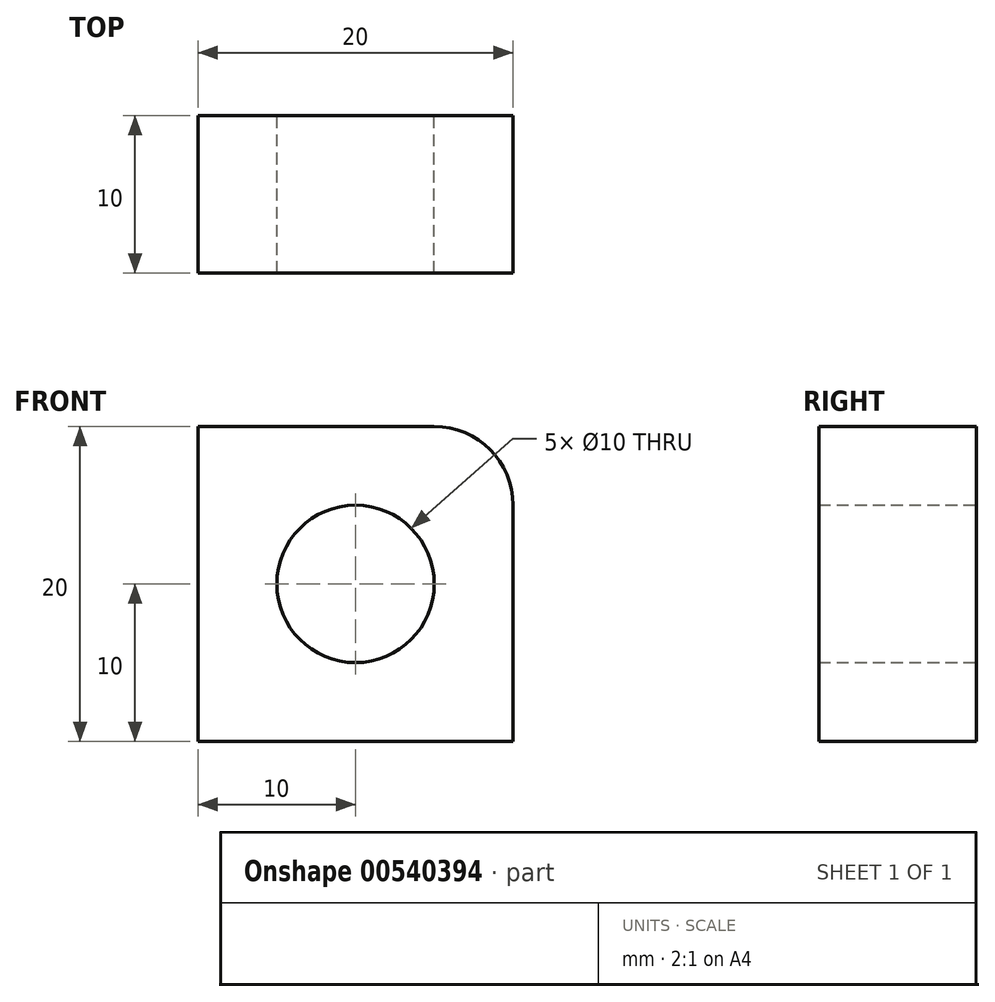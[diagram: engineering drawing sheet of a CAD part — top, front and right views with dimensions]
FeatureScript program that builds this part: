
annotation { "Feature Type Name" : "Feature", "Feature Type Description" : "" }
export const myFeature = defineFeature(function(context is Context, id is Id, definition is map)
    precondition{}
    {
        {
            var Q0;
            Q0=qCreatedBy(makeId("Front.planeOp"),FACE);
            var sketch = newSketch(context, id + "F0", { "sketchPlane" : qUnion([Q0])});
            skLineSegment(sketch, "E0.bottom", {"start": v(5, 10) * mm, "end": v(-10, 10) * mm});
            skLineSegment(sketch, "E0.top", {"start": v(10, -10) * mm, "end": v(-10, -10) * mm});
            skLineSegment(sketch, "E0.left", {"start": v(10, 5) * mm, "end": v(10, -10) * mm});
            skLineSegment(sketch, "E0.right", {"start": v(-10, 10) * mm, "end": v(-10, -10) * mm});
            skPoint(sketch, "E0.middle", {"position": v(0, 0) * mm});
            skPoint(sketch, "E1.visualSharp", {"position": v(10, 10) * mm});
            skArc(sketch, "E1.filletArc", {"start": v(10, 5) * mm, "mid": v(8.54, 8.54) * mm, "end": v(5, 10) * mm});
            skCircle(sketch, "E2", {"center": v(0, 0) * mm, "radius": 5 * mm});
            skSolve(sketch);
        }
        {
            var Q0;
            Q0=makeQuery(id+"F0.imprint","IMPRINT",FACE,{"disambiguationData":[TD([[makeQuery(id+"F0.imprint","IMPRINT",EDGE,{"derivedFrom":sQuery(id+"F0.wireOp",EDGE,"E0.bottom")}),1.0]])]});
            extrude(context, id + "F1", {"entities" : qUnion([Q0]), "depth" : 10 * mm, "offsetDistance" : 25 * mm});
        }
    });
